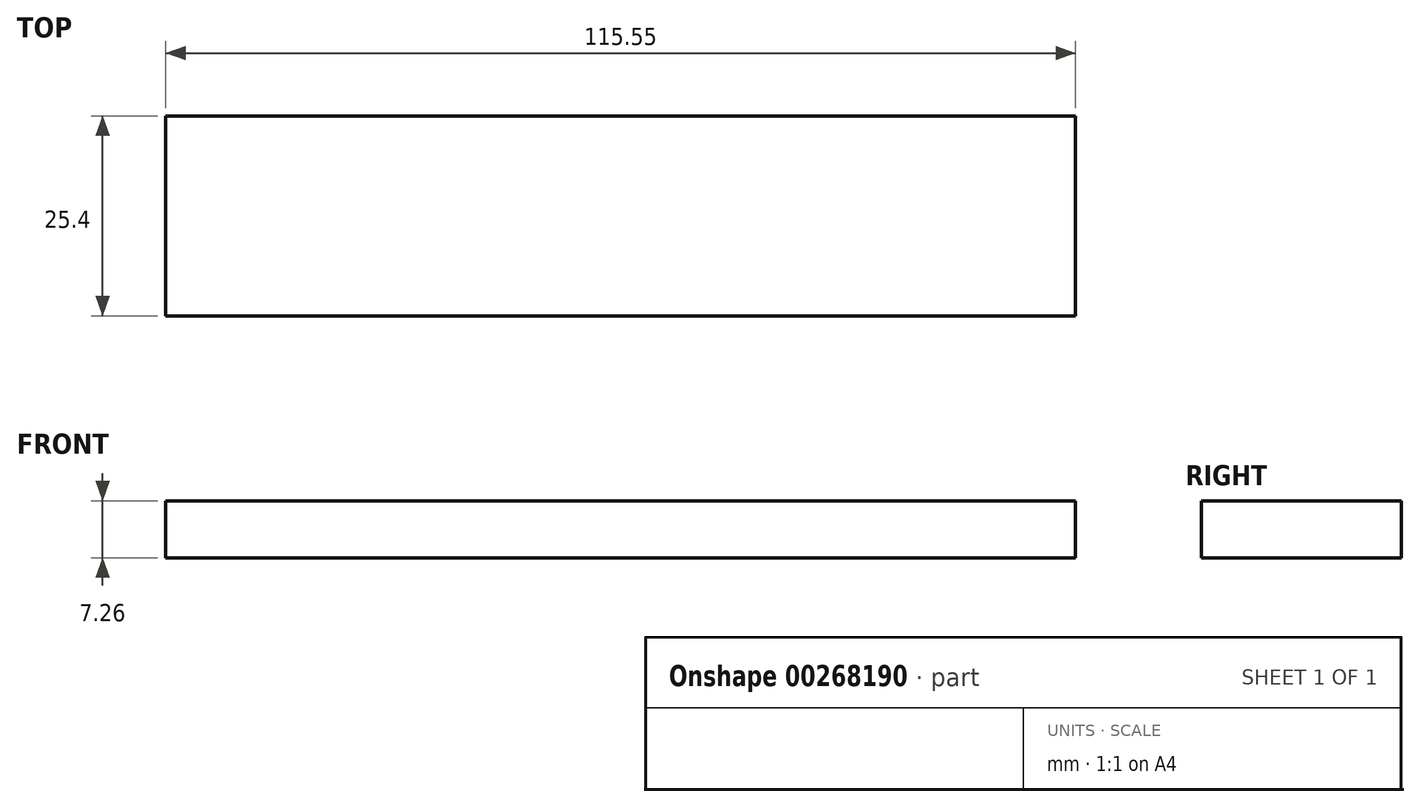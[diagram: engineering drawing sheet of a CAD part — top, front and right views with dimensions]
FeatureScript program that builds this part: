
annotation { "Feature Type Name" : "Feature", "Feature Type Description" : "" }
export const myFeature = defineFeature(function(context is Context, id is Id, definition is map)
    precondition{}
    {
        {
            var Q0;
            Q0=qCreatedBy(makeId("Front.planeOp"),FACE);
            var sketch = newSketch(context, id + "F0", { "sketchPlane" : qUnion([Q0])});
            skLineSegment(sketch, "E0.bottom", {"start": v(49.58, 42.94) * mm, "end": v(-65.97, 42.94) * mm});
            skLineSegment(sketch, "E0.top", {"start": v(49.58, 35.68) * mm, "end": v(-65.97, 35.68) * mm});
            skLineSegment(sketch, "E0.left", {"start": v(49.58, 42.94) * mm, "end": v(49.58, 35.68) * mm});
            skLineSegment(sketch, "E0.right", {"start": v(-65.97, 42.94) * mm, "end": v(-65.97, 35.68) * mm});
            skLineSegment(sketch, "E1.bottom", {"start": v(49.58, 19.92) * mm, "end": v(-64.93, 19.92) * mm});
            skLineSegment(sketch, "E1.top", {"start": v(49.58, 25.72) * mm, "end": v(-64.93, 25.72) * mm});
            skLineSegment(sketch, "E1.left", {"start": v(49.58, 19.92) * mm, "end": v(49.58, 25.72) * mm});
            skLineSegment(sketch, "E1.right", {"start": v(-64.93, 19.92) * mm, "end": v(-64.93, 25.72) * mm});
            skSolve(sketch);
        }
        {
            var Q0;
            Q0=makeQuery(id+"F0.imprint","IMPRINT",FACE,{"disambiguationData":[TD([[makeQuery(id+"F0.imprint","IMPRINT",EDGE,{"derivedFrom":sQuery(id+"F0.wireOp",EDGE,"E0.bottom")}),1.0]])]});
            var Q1;
            Q1=makeQuery(id+"F0.imprint","IMPRINT",FACE,{"disambiguationData":[TD([[makeQuery(id+"F0.imprint","IMPRINT",EDGE,{"derivedFrom":sQuery(id+"F0.wireOp",EDGE,"E0.bottom")}),1.0]])]});
            extrude(context, id + "F1", {"entities" : qUnion([Q0, Q1]), "depth" : 25.4 * mm});
        }
    });
